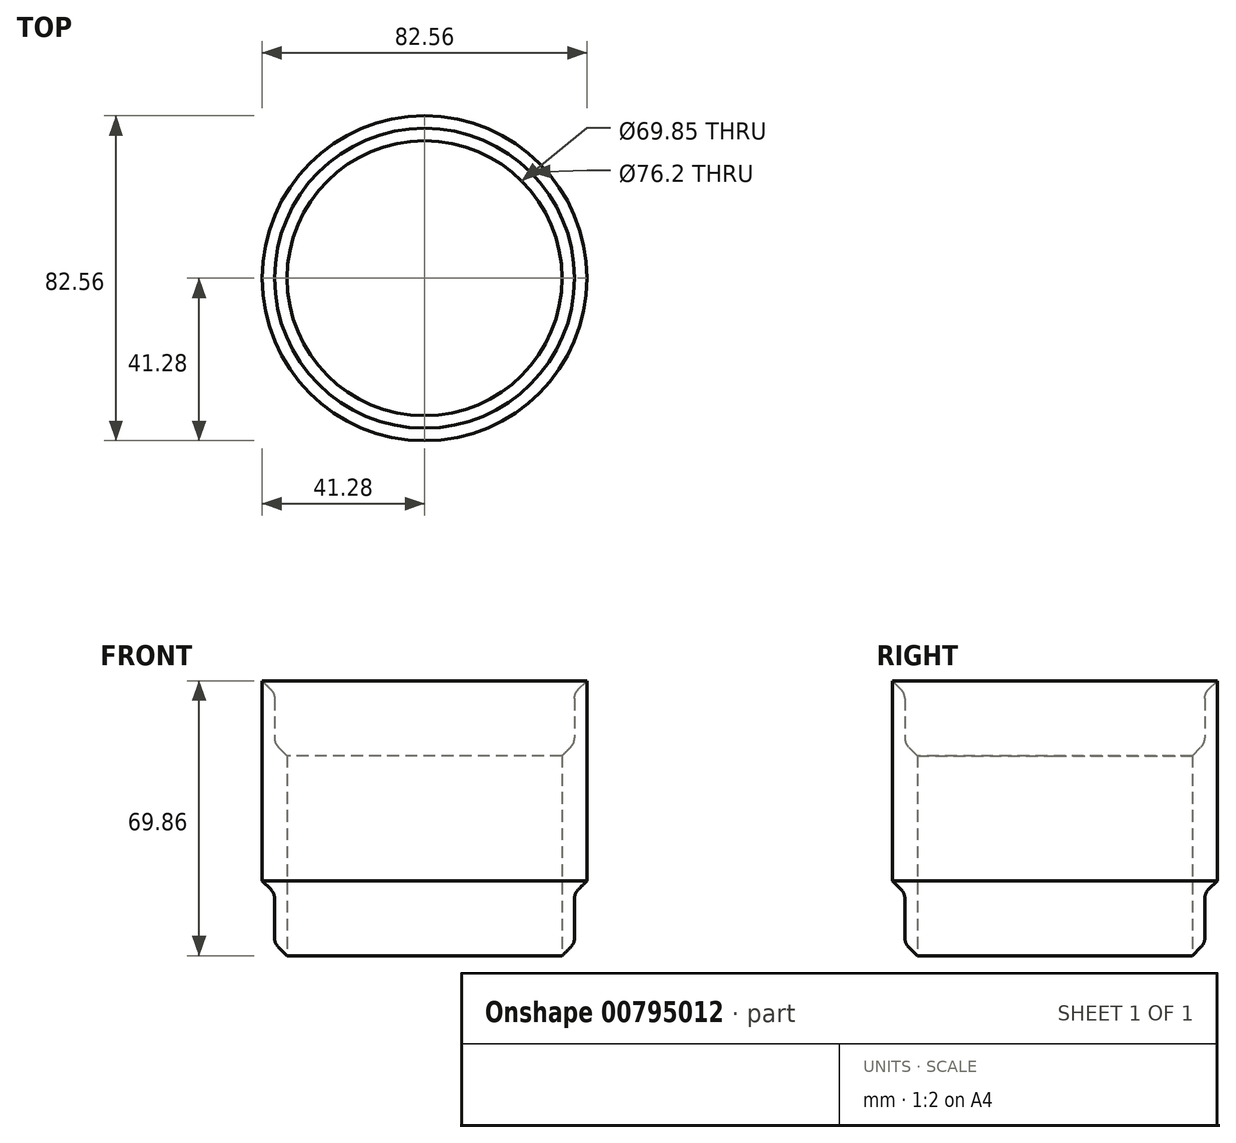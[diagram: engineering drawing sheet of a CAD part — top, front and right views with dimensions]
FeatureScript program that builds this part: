
annotation { "Feature Type Name" : "Feature", "Feature Type Description" : "" }
export const myFeature = defineFeature(function(context is Context, id is Id, definition is map)
    precondition{}
    {
        {
            var Q0;
            Q0=qCreatedBy(makeId("Front.planeOp"),FACE);
            var sketch = newSketch(context, id + "F0", { "sketchPlane" : qUnion([Q0])});
            skLineSegment(sketch, "E0", {"start": v(-41.27, 66.67) * mm, "end": v(-41.27, 15.87) * mm});
            skLineSegment(sketch, "E1", {"start": v(-41.27, 15.87) * mm, "end": v(-38.1, 12.7) * mm});
            skLineSegment(sketch, "E2", {"start": v(-38.1, 12.7) * mm, "end": v(-38.1, 0) * mm});
            skPoint(sketch, "E3", {"position": v(0, 0) * mm});
            skLineSegment(sketch, "E4", {"start": v(0, 0) * mm, "end": v(0, 66.67) * mm});
            skLineSegment(sketch, "E5", {"start": v(-41.27, 66.67) * mm, "end": v(-38.1, 63.5) * mm});
            skLineSegment(sketch, "E6", {"start": v(-38.1, 63.5) * mm, "end": v(-38.1, 50.8) * mm});
            skLineSegment(sketch, "E7", {"start": v(-38.1, 50.8) * mm, "end": v(-34.93, 50.8) * mm});
            skLineSegment(sketch, "E8", {"start": v(-34.92, -3.18) * mm, "end": v(-38.1, 0) * mm});
            skLineSegment(sketch, "E9", {"start": v(-34.93, 50.8) * mm, "end": v(-34.92, -3.18) * mm});
            skLineSegment(sketch, "E10", {"start": v(0, 0) * mm, "end": v(3.18, 0) * mm, "construction": true});
            skLineSegment(sketch, "E11", {"start": v(3.18, 0) * mm, "end": v(3.18, 5.5) * mm, "construction": true});
            skLineSegment(sketch, "E12", {"start": v(0, 0) * mm, "end": v(3.17, 5.5) * mm, "construction": true});
            skLineSegment(sketch, "E13", {"start": v(3.17, 5.5) * mm, "end": v(6.35, 5.5) * mm, "construction": true});
            skLineSegment(sketch, "E14", {"start": v(6.35, 5.5) * mm, "end": v(6.35, 11) * mm, "construction": true});
            skLineSegment(sketch, "E15", {"start": v(6.35, 11) * mm, "end": v(3.17, 5.5) * mm, "construction": true});
            skLineSegment(sketch, "E16", {"start": v(6.35, 11) * mm, "end": v(6.35, 23.7) * mm, "construction": true});
            skLineSegment(sketch, "E17", {"start": v(0, 0) * mm, "end": v(12.7, 0) * mm, "construction": true});
            skLineSegment(sketch, "E18", {"start": v(12.7, 0) * mm, "end": v(12.7, 50.8) * mm, "construction": true});
            skSolve(sketch);
        }
        {
            var Q0;
            Q0=makeQuery(id+"F0.imprint","IMPRINT",FACE,{"disambiguationData":[TD([[makeQuery(id+"F0.imprint","IMPRINT",EDGE,{"derivedFrom":sQuery(id+"F0.wireOp",EDGE,"E0")}),1.0]])]});
            var Q1;
            Q1=sQuery(id+"F0.wireOp",EDGE,"E4");
            revolve(context, id + "F1", {"surfaceOperationType" : NewSurfaceOperationType.NEW, "entities" : qUnion([Q0]), "axis" : qUnion([Q1]), "revolveType" : RevolveType.FULL});
        }
        {
            var Q0;
            Q0=makeQuery(id+"F1.opRevolve","SWEPT_EDGE",EDGE,{"disambiguationData":[OSD([sQuery(id+"F0.wireOp",EDGE,"E5"),sQuery(id+"F0.wireOp",EDGE,"E6")])]});
            fillet(context, id + "F2", {"entities" : qUnion([Q0]), "tangentPropagation" : true, "radius" : 3.17 * mm, "defaultsChanged" : true, "vertexSettings" : [], "allowEdgeOverflow" : false});
        }
        {
            var Q0;
            Q0=makeQuery(id+"F1.opRevolve","SWEPT_EDGE",EDGE,{"disambiguationData":[OSD([sQuery(id+"F0.wireOp",EDGE,"E7"),sQuery(id+"F0.wireOp",EDGE,"E9")])]});
            chamfer(context, id + "F3", {"entities" : qUnion([Q0]), "width" : 3.17 * mm, "tangentPropagation" : true});
        }
        {
            var Q0;
            Q0=makeQuery(id+"F1.opRevolve","SWEPT_EDGE",EDGE,{"disambiguationData":[OSD([sQuery(id+"F0.wireOp",EDGE,"E2"),sQuery(id+"F0.wireOp",EDGE,"E8")])]});
            fillet(context, id + "F4", {"entities" : qUnion([Q0]), "tangentPropagation" : true, "radius" : 3.17 * mm, "defaultsChanged" : true, "vertexSettings" : [], "allowEdgeOverflow" : false});
        }
        {
            var Q0;
            Q0=makeQuery(id+"F1.opRevolve","SWEPT_EDGE",EDGE,{"disambiguationData":[OSD([sQuery(id+"F0.wireOp",EDGE,"E1"),sQuery(id+"F0.wireOp",EDGE,"E2")])]});
            fillet(context, id + "F5", {"entities" : qUnion([Q0]), "tangentPropagation" : true, "radius" : 3.17 * mm, "defaultsChanged" : true, "vertexSettings" : [], "allowEdgeOverflow" : false});
        }
        {
            var Q0;
            Q0=makeQuery(id+"F3.opChamfer","BLEND_EDGE",EDGE,{"blendedFrom":[makeQuery(id+"F1.opRevolve","SWEPT_EDGE",EDGE,{"disambiguationData":[OSD([sQuery(id+"F0.wireOp",EDGE,"E7"),sQuery(id+"F0.wireOp",EDGE,"E9")])]}),makeQuery(id+"F1.opRevolve","SWEPT_FACE",FACE,{"disambiguationData":[OSD([sQuery(id+"F0.wireOp",EDGE,"E6")])]})],"blendedInto":[makeQuery(id+"F1.opRevolve","SWEPT_FACE",FACE,{"disambiguationData":[OSD([sQuery(id+"F0.wireOp",EDGE,"E6")])]})]});
            fillet(context, id + "F6", {"entities" : qUnion([Q0]), "tangentPropagation" : true, "radius" : 3.17 * mm, "defaultsChanged" : true, "vertexSettings" : [], "allowEdgeOverflow" : false});
        }
    });
